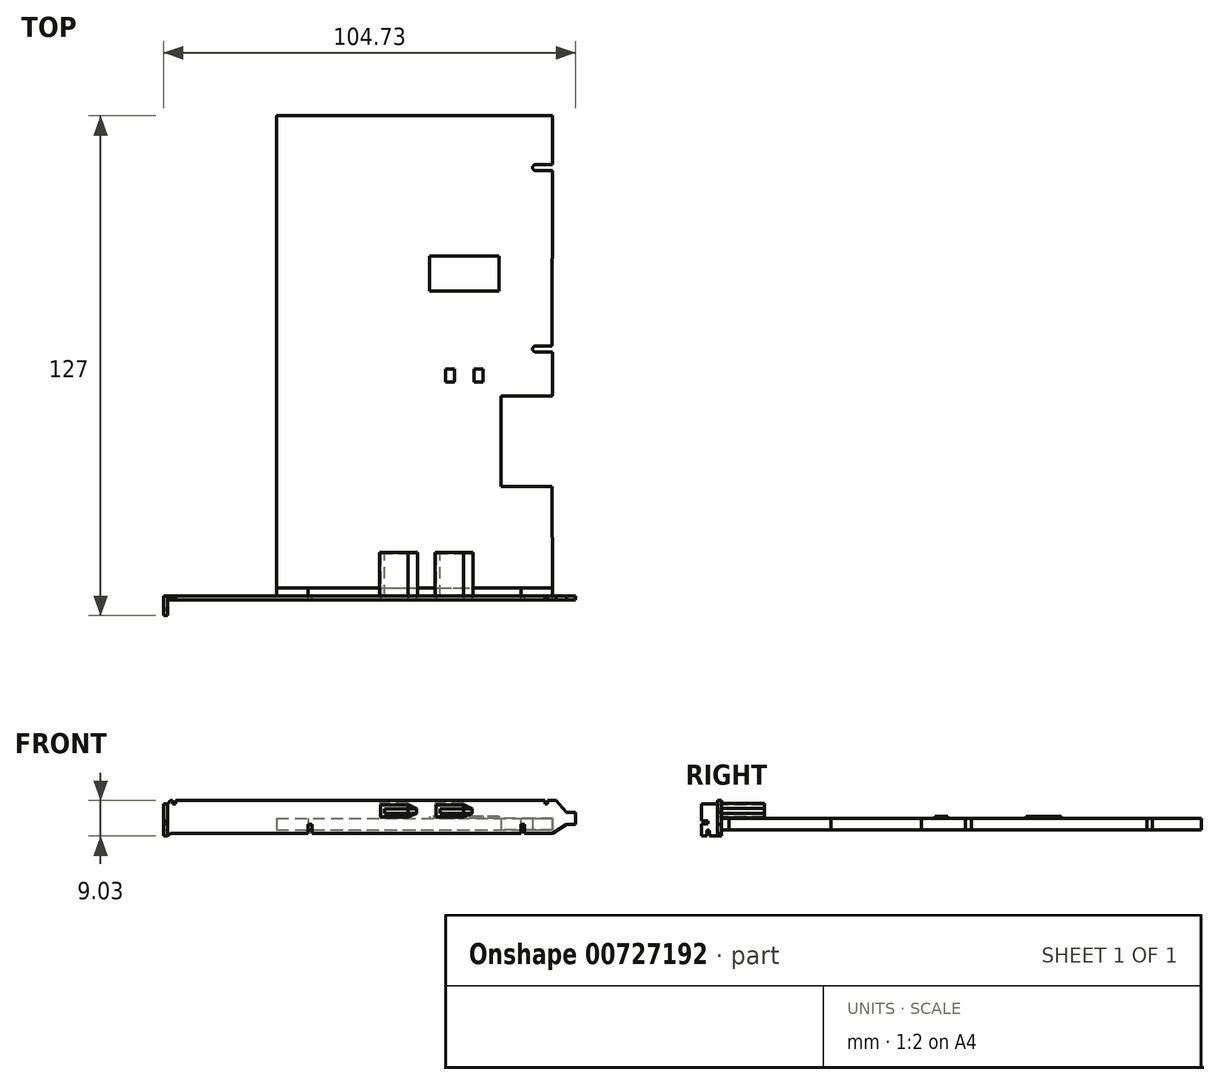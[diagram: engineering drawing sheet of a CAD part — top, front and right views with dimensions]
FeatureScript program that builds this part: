
annotation { "Feature Type Name" : "Feature", "Feature Type Description" : "" }
export const myFeature = defineFeature(function(context is Context, id is Id, definition is map)
    precondition{}
    {
        {
            var Q0;
            Q0=qCreatedBy(makeId("Top.planeOp"),FACE);
            var sketch = newSketch(context, id + "F0", { "sketchPlane" : qUnion([Q0])});
            skLineSegment(sketch, "E0.bottom", {"start": v(-33.4, 60) * mm, "end": v(36.6, 60) * mm});
            skLineSegment(sketch, "E0.top", {"start": v(-33.4, -60) * mm, "end": v(36.6, -60) * mm});
            skLineSegment(sketch, "E0.left", {"start": v(-33.4, 60) * mm, "end": v(-33.4, -60) * mm});
            skPoint(sketch, "E0.middle", {"position": v(1.6, 0) * mm});
            skLineSegment(sketch, "E1.bottom", {"start": v(36.55, -11.18) * mm, "end": v(36.6, -11.18) * mm});
            skLineSegment(sketch, "E1.top", {"start": v(36.6, -26.7) * mm, "end": v(36.6, -26.7) * mm});
            skLineSegment(sketch, "E2", {"start": v(36.6, 60) * mm, "end": v(36.6, 47.56) * mm});
            skLineSegment(sketch, "E3.bottom", {"start": v(36.55, -11.18) * mm, "end": v(23.55, -11.18) * mm});
            skLineSegment(sketch, "E3.top", {"start": v(36.55, -34.18) * mm, "end": v(23.55, -34.18) * mm});
            skLineSegment(sketch, "E3.right", {"start": v(23.55, -11.18) * mm, "end": v(23.55, -34.18) * mm});
            skLineSegment(sketch, "E4", {"start": v(36.6, -60) * mm, "end": v(36.55, -34.18) * mm});
            skLineSegment(sketch, "E5", {"start": v(36.6, 0) * mm, "end": v(32.35, 0) * mm});
            skLineSegment(sketch, "E6", {"start": v(31.6, 0.75) * mm, "end": v(31.6, 0.75) * mm});
            skLineSegment(sketch, "E7", {"start": v(32.35, 1.5) * mm, "end": v(36.55, 1.5) * mm});
            skLineSegment(sketch, "E8", {"start": v(36.6, 47.56) * mm, "end": v(32.35, 47.56) * mm});
            skLineSegment(sketch, "E9", {"start": v(31.6, 46.81) * mm, "end": v(31.6, 46.81) * mm});
            skLineSegment(sketch, "E10", {"start": v(32.35, 46.06) * mm, "end": v(36.6, 46.06) * mm});
            skLineSegment(sketch, "E11.trimOffspring", {"start": v(36.6, 0) * mm, "end": v(36.6, -11.18) * mm});
            skLineSegment(sketch, "E12", {"start": v(36.55, 1.5) * mm, "end": v(36.6, 46.06) * mm});
            skPoint(sketch, "E13.visualSharp", {"position": v(31.6, 47.56) * mm});
            skArc(sketch, "E13.filletArc", {"start": v(32.35, 47.56) * mm, "mid": v(31.82, 47.34) * mm, "end": v(31.6, 46.81) * mm});
            skPoint(sketch, "E14.visualSharp", {"position": v(31.6, 46.06) * mm});
            skArc(sketch, "E14.filletArc", {"start": v(31.6, 46.81) * mm, "mid": v(31.82, 46.28) * mm, "end": v(32.35, 46.06) * mm});
            skPoint(sketch, "E15.visualSharp", {"position": v(31.6, 0) * mm});
            skArc(sketch, "E15.filletArc", {"start": v(31.6, 0.75) * mm, "mid": v(31.82, 0.22) * mm, "end": v(32.35, 0) * mm});
            skPoint(sketch, "E16.visualSharp", {"position": v(31.6, 1.5) * mm});
            skArc(sketch, "E16.filletArc", {"start": v(32.35, 1.5) * mm, "mid": v(31.82, 1.28) * mm, "end": v(31.6, 0.75) * mm});
            skSolve(sketch);
        }
        {
            var Q0;
            Q0 = qSketchRegion(id + "F0", true);
            extrude(context, id + "F1", {"entities" : qUnion([Q0]), "depth" : 3 * mm, "offsetDistance" : 25 * mm});
        }
        {
            var Q0;
            Q0=makeQuery(id+"F1.opExtrude","SWEPT_FACE",FACE,{"disambiguationData":[OSD([sQuery(id+"F0.wireOp",EDGE,"E0.top")])]});
            var sketch = newSketch(context, id + "F2", { "sketchPlane" : qUnion([Q0])});
            skLineSegment(sketch, "E17.bottom", {"start": v(36.6, 0) * mm, "end": v(28.6, 0) * mm});
            skLineSegment(sketch, "E17.top", {"start": v(36.6, 3) * mm, "end": v(28.6, 3) * mm});
            skLineSegment(sketch, "E17.left", {"start": v(36.6, 0) * mm, "end": v(36.6, 3) * mm});
            skLineSegment(sketch, "E17.right", {"start": v(28.6, 0) * mm, "end": v(28.6, 3) * mm});
            skLineSegment(sketch, "E18.bottom", {"start": v(-33.4, 3) * mm, "end": v(-25.4, 3) * mm});
            skLineSegment(sketch, "E18.top", {"start": v(-33.4, 0) * mm, "end": v(-25.4, 0) * mm});
            skLineSegment(sketch, "E18.left", {"start": v(-33.4, 3) * mm, "end": v(-33.4, 0) * mm});
            skLineSegment(sketch, "E18.right", {"start": v(-25.4, 3) * mm, "end": v(-25.4, 0) * mm});
            skSolve(sketch);
        }
        {
            var Q0;
            Q0 = qSketchRegion(id + "F2", true);
            extrude(context, id + "F3", {"entities" : qUnion([Q0]), "depth" : 2 * mm, "offsetDistance" : 25 * mm});
        }
        {
            var Q0;
            Q0=makeQuery(id+"F3.opExtrude","CAP_FACE",FACE,{"disambiguationData":[OSD([sQuery(id+"F2.wireOp",EDGE,"E18.bottom"),sQuery(id+"F2.wireOp",EDGE,"E18.top"),sQuery(id+"F2.wireOp",EDGE,"E18.left"),sQuery(id+"F2.wireOp",EDGE,"E18.right")])],"isStart":false});
            var sketch = newSketch(context, id + "F4", { "sketchPlane" : qUnion([Q0])});
            skLineSegment(sketch, "E19", {"start": v(-25.4, 0) * mm, "end": v(-25.4, 1.5) * mm});
            skLineSegment(sketch, "E20", {"start": v(-25.4, 1.5) * mm, "end": v(-24.4, 1.5) * mm});
            skLineSegment(sketch, "E21", {"start": v(-24.4, 1.5) * mm, "end": v(-24.4, -0.8) * mm});
            skLineSegment(sketch, "E22", {"start": v(28.6, 0) * mm, "end": v(28.6, 0.1) * mm});
            skPoint(sketch, "E23.end.orphan", {"position": v(28.6, -0.8) * mm});
            skLineSegment(sketch, "E24", {"start": v(-24.4, -0.8) * mm, "end": v(28.6, -0.8) * mm});
            skLineSegment(sketch, "E25", {"start": v(28.6, -0.8) * mm, "end": v(28.6, 1.5) * mm});
            skLineSegment(sketch, "E26", {"start": v(28.6, 1.5) * mm, "end": v(29.6, 1.5) * mm});
            skLineSegment(sketch, "E27", {"start": v(29.6, 1.5) * mm, "end": v(29.6, 0) * mm});
            skPoint(sketch, "E27.endSnap0", {"position": v(-29.4, 0) * mm});
            skLineSegment(sketch, "E28", {"start": v(-25.4, 0) * mm, "end": v(-25.4, -0.8) * mm});
            skLineSegment(sketch, "E29", {"start": v(-25.4, -0.8) * mm, "end": v(-60.4, -0.8) * mm});
            skLineSegment(sketch, "E30", {"start": v(29.6, 0) * mm, "end": v(29.6, -0.8) * mm});
            skLineSegment(sketch, "E31", {"start": v(29.6, -0.8) * mm, "end": v(36.6, -0.8) * mm});
            skLineSegment(sketch, "E32", {"start": v(36.6, -0.8) * mm, "end": v(40.24, 1.5) * mm});
            skLineSegment(sketch, "E33", {"start": v(40.24, 1.5) * mm, "end": v(42.54, 1.5) * mm});
            skLineSegment(sketch, "E34", {"start": v(42.54, 1.5) * mm, "end": v(42.54, 4.54) * mm});
            skLineSegment(sketch, "E35", {"start": v(42.54, 4.54) * mm, "end": v(40.24, 4.54) * mm});
            skLineSegment(sketch, "E36", {"start": v(40.24, 4.54) * mm, "end": v(37.54, 7.5) * mm});
            skLineSegment(sketch, "E37", {"start": v(37.54, 7.5) * mm, "end": v(35.44, 7.5) * mm});
            skLineSegment(sketch, "E38", {"start": v(35.44, 7.5) * mm, "end": v(35.44, 6.6) * mm});
            skLineSegment(sketch, "E39", {"start": v(35.44, 6.6) * mm, "end": v(34.74, 6.6) * mm});
            skLineSegment(sketch, "E40", {"start": v(34.74, 6.6) * mm, "end": v(34.74, 7.5) * mm});
            skLineSegment(sketch, "E41", {"start": v(34.74, 7.5) * mm, "end": v(-59.13, 7.5) * mm});
            skLineSegment(sketch, "E42", {"start": v(-59.13, 7.5) * mm, "end": v(-59.13, 6.6) * mm});
            skLineSegment(sketch, "E43", {"start": v(-59.13, 6.6) * mm, "end": v(-59.83, 6.6) * mm});
            skLineSegment(sketch, "E44", {"start": v(-59.83, 6.6) * mm, "end": v(-59.83, 7.5) * mm});
            skLineSegment(sketch, "E45.trimOffspring", {"start": v(-59.83, 7.5) * mm, "end": v(-60.4, 7.5) * mm});
            skLineSegment(sketch, "E46", {"start": v(-60.4, -0.8) * mm, "end": v(-61.16, -1.54) * mm});
            skLineSegment(sketch, "E47", {"start": v(-60.4, 7.5) * mm, "end": v(-61.16, 6.6) * mm});
            skLineSegment(sketch, "E48", {"start": v(-61.16, 6.6) * mm, "end": v(-62.19, 6.6) * mm});
            skLineSegment(sketch, "E49", {"start": v(-62.19, 6.6) * mm, "end": v(-62.19, -1.54) * mm});
            skLineSegment(sketch, "E50", {"start": v(-62.19, -1.54) * mm, "end": v(-61.16, -1.54) * mm});
            skSolve(sketch);
        }
        {
            var Q0;
            Q0 = qSketchRegion(id + "F4", true);
            extrude(context, id + "F5", {"entities" : qUnion([Q0]), "depth" : 1 * mm, "offsetDistance" : 25 * mm});
        }
        {
            var Q0;
            Q0=makeQuery(id+"F5.opExtrude","CAP_FACE",FACE,{"disambiguationData":[OSD([sQuery(id+"F4.wireOp",EDGE,"E19"),sQuery(id+"F4.wireOp",EDGE,"E20"),sQuery(id+"F4.wireOp",EDGE,"E21"),sQuery(id+"F4.wireOp",EDGE,"E24"),sQuery(id+"F4.wireOp",EDGE,"E25"),sQuery(id+"F4.wireOp",EDGE,"E26"),sQuery(id+"F4.wireOp",EDGE,"E27"),sQuery(id+"F4.wireOp",EDGE,"E28"),sQuery(id+"F4.wireOp",EDGE,"E29"),sQuery(id+"F4.wireOp",EDGE,"E30"),sQuery(id+"F4.wireOp",EDGE,"E31"),sQuery(id+"F4.wireOp",EDGE,"E32"),sQuery(id+"F4.wireOp",EDGE,"E33"),sQuery(id+"F4.wireOp",EDGE,"E34"),sQuery(id+"F4.wireOp",EDGE,"E35"),sQuery(id+"F4.wireOp",EDGE,"E36"),sQuery(id+"F4.wireOp",EDGE,"E37"),sQuery(id+"F4.wireOp",EDGE,"E38"),sQuery(id+"F4.wireOp",EDGE,"E39"),sQuery(id+"F4.wireOp",EDGE,"E40"),sQuery(id+"F4.wireOp",EDGE,"E41"),sQuery(id+"F4.wireOp",EDGE,"E42"),sQuery(id+"F4.wireOp",EDGE,"E43"),sQuery(id+"F4.wireOp",EDGE,"E44"),sQuery(id+"F4.wireOp",EDGE,"E45.trimOffspring"),sQuery(id+"F4.wireOp",EDGE,"E46"),sQuery(id+"F4.wireOp",EDGE,"E47"),sQuery(id+"F4.wireOp",EDGE,"E48"),sQuery(id+"F4.wireOp",EDGE,"E49"),sQuery(id+"F4.wireOp",EDGE,"E50")])],"isStart":false});
            var sketch = newSketch(context, id + "F6", { "sketchPlane" : qUnion([Q0])});
            skLineSegment(sketch, "E51", {"start": v(16.19, 3.63) * mm, "end": v(16.19, 3.63) * mm});
            skLineSegment(sketch, "E52", {"start": v(16.19, 5.43) * mm, "end": v(16.19, 4.3) * mm});
            skLineSegment(sketch, "E53", {"start": v(16.19, 4.3) * mm, "end": v(14.06, 3.3) * mm});
            skLineSegment(sketch, "E54.MirrorCS", {"start": v(16.19, 5.43) * mm, "end": v(14.06, 6.43) * mm});
            skPoint(sketch, "E55.orphan", {"position": v(16.19, 3.63) * mm});
            skPoint(sketch, "E56.orphan", {"position": v(16.19, 6.1) * mm});
            skLineSegment(sketch, "E57", {"start": v(14.06, 3.3) * mm, "end": v(7.06, 3.3) * mm});
            skLineSegment(sketch, "E58", {"start": v(14.06, 6.43) * mm, "end": v(7.06, 6.43) * mm});
            skLineSegment(sketch, "E59", {"start": v(7.06, 6.43) * mm, "end": v(7.06, 3.3) * mm});
            skPoint(sketch, "E60.end.orphan", {"position": v(18.65, 3.3) * mm});
            skLineSegment(sketch, "E61", {"start": v(0, 6.43) * mm, "end": v(-7, 6.43) * mm});
            skLineSegment(sketch, "E62", {"start": v(0, 3.3) * mm, "end": v(-7, 3.3) * mm});
            skLineSegment(sketch, "E63", {"start": v(-7, 6.43) * mm, "end": v(-7, 3.3) * mm});
            skLineSegment(sketch, "E64", {"start": v(0, 3.3) * mm, "end": v(2.1, 4.3) * mm});
            skLineSegment(sketch, "E65", {"start": v(0, 6.43) * mm, "end": v(2.1, 5.43) * mm});
            skLineSegment(sketch, "E66", {"start": v(2.1, 5.43) * mm, "end": v(2.1, 4.3) * mm});
            skPoint(sketch, "E67.orphan", {"position": v(-2.37, 5.43) * mm});
            skPoint(sketch, "E68.orphan", {"position": v(-2.37, 4.3) * mm});
            skSolve(sketch);
        }
        {
            var Q0;
            Q0 = qSketchRegion(id + "F6", true);
            extrude(context, id + "F7", {"entities" : qUnion([Q0]), "operationType" : NewBodyOperationType.REMOVE, "oppositeDirection" : true, "depth" : 25 * mm, "offsetDistance" : 25 * mm});
        }
        {
            var Q0;
            Q0=makeQuery(id+"F5.opExtrude","CAP_FACE",FACE,{"disambiguationData":[OSD([sQuery(id+"F4.wireOp",EDGE,"E19"),sQuery(id+"F4.wireOp",EDGE,"E20"),sQuery(id+"F4.wireOp",EDGE,"E21"),sQuery(id+"F4.wireOp",EDGE,"E24"),sQuery(id+"F4.wireOp",EDGE,"E25"),sQuery(id+"F4.wireOp",EDGE,"E26"),sQuery(id+"F4.wireOp",EDGE,"E27"),sQuery(id+"F4.wireOp",EDGE,"E28"),sQuery(id+"F4.wireOp",EDGE,"E29"),sQuery(id+"F4.wireOp",EDGE,"E30"),sQuery(id+"F4.wireOp",EDGE,"E31"),sQuery(id+"F4.wireOp",EDGE,"E32"),sQuery(id+"F4.wireOp",EDGE,"E33"),sQuery(id+"F4.wireOp",EDGE,"E34"),sQuery(id+"F4.wireOp",EDGE,"E35"),sQuery(id+"F4.wireOp",EDGE,"E36"),sQuery(id+"F4.wireOp",EDGE,"E37"),sQuery(id+"F4.wireOp",EDGE,"E38"),sQuery(id+"F4.wireOp",EDGE,"E39"),sQuery(id+"F4.wireOp",EDGE,"E40"),sQuery(id+"F4.wireOp",EDGE,"E41"),sQuery(id+"F4.wireOp",EDGE,"E42"),sQuery(id+"F4.wireOp",EDGE,"E43"),sQuery(id+"F4.wireOp",EDGE,"E44"),sQuery(id+"F4.wireOp",EDGE,"E45.trimOffspring"),sQuery(id+"F4.wireOp",EDGE,"E46"),sQuery(id+"F4.wireOp",EDGE,"E47"),sQuery(id+"F4.wireOp",EDGE,"E48"),sQuery(id+"F4.wireOp",EDGE,"E49"),sQuery(id+"F4.wireOp",EDGE,"E50")])],"isStart":true});
            var sketch = newSketch(context, id + "F8", { "sketchPlane" : qUnion([Q0])});
            skLineSegment(sketch, "E69", {"start": v(0, 6.43) * mm, "end": v(7, 6.43) * mm});
            skLineSegment(sketch, "E70", {"start": v(7, 6.43) * mm, "end": v(7, 3.3) * mm});
            skLineSegment(sketch, "E71", {"start": v(7, 3.3) * mm, "end": v(0, 3.3) * mm});
            skLineSegment(sketch, "E72", {"start": v(0, 3.3) * mm, "end": v(-2.1, 4.3) * mm});
            skLineSegment(sketch, "E73", {"start": v(-2.1, 4.3) * mm, "end": v(-2.1, 5.43) * mm});
            skLineSegment(sketch, "E74", {"start": v(-2.1, 5.43) * mm, "end": v(0, 6.43) * mm});
            skLineSegment(sketch, "E75", {"start": v(3.31, 6.73) * mm, "end": v(7.3, 6.73) * mm});
            skLineSegment(sketch, "E76", {"start": v(7.3, 6.73) * mm, "end": v(7.3, 3.1) * mm});
            skLineSegment(sketch, "E77", {"start": v(7.3, 3.1) * mm, "end": v(0, 3.1) * mm});
            skLineSegment(sketch, "E78", {"start": v(0, 3.1) * mm, "end": v(-2.4, 4.3) * mm});
            skLineSegment(sketch, "E79", {"start": v(-2.4, 4.3) * mm, "end": v(-2.4, 5.56) * mm});
            skLineSegment(sketch, "E80", {"start": v(-2.4, 5.56) * mm, "end": v(0.06, 6.73) * mm});
            skLineSegment(sketch, "E81", {"start": v(0.06, 6.73) * mm, "end": v(3.31, 6.73) * mm});
            skPoint(sketch, "E82.end.orphan", {"position": v(3.24, 3.1) * mm});
            skPoint(sketch, "E83.end.orphan", {"position": v(7.3, 4.86) * mm});
            skPoint(sketch, "E83.start.orphan", {"position": v(7, 4.86) * mm});
            skPoint(sketch, "E84.orphan", {"position": v(-1.05, 5.93) * mm});
            skPoint(sketch, "E85.end.orphan", {"position": v(-2.4, 4.86) * mm});
            skPoint(sketch, "E85.start.orphan", {"position": v(-2.1, 4.86) * mm});
            skSolve(sketch);
        }
        {
            var Q0;
            Q0 = qSketchRegion(id + "F8", true);
            extrude(context, id + "F9", {"entities" : qUnion([Q0]), "operationType" : NewBodyOperationType.ADD, "depth" : 11 * mm, "offsetDistance" : 25 * mm});
        }
        {
            var Q0;
            Q0=makeQuery(id+"F5.opExtrude","CAP_FACE",FACE,{"disambiguationData":[OSD([sQuery(id+"F4.wireOp",EDGE,"E19"),sQuery(id+"F4.wireOp",EDGE,"E20"),sQuery(id+"F4.wireOp",EDGE,"E21"),sQuery(id+"F4.wireOp",EDGE,"E24"),sQuery(id+"F4.wireOp",EDGE,"E25"),sQuery(id+"F4.wireOp",EDGE,"E26"),sQuery(id+"F4.wireOp",EDGE,"E27"),sQuery(id+"F4.wireOp",EDGE,"E28"),sQuery(id+"F4.wireOp",EDGE,"E29"),sQuery(id+"F4.wireOp",EDGE,"E30"),sQuery(id+"F4.wireOp",EDGE,"E31"),sQuery(id+"F4.wireOp",EDGE,"E32"),sQuery(id+"F4.wireOp",EDGE,"E33"),sQuery(id+"F4.wireOp",EDGE,"E34"),sQuery(id+"F4.wireOp",EDGE,"E35"),sQuery(id+"F4.wireOp",EDGE,"E36"),sQuery(id+"F4.wireOp",EDGE,"E37"),sQuery(id+"F4.wireOp",EDGE,"E38"),sQuery(id+"F4.wireOp",EDGE,"E39"),sQuery(id+"F4.wireOp",EDGE,"E40"),sQuery(id+"F4.wireOp",EDGE,"E41"),sQuery(id+"F4.wireOp",EDGE,"E42"),sQuery(id+"F4.wireOp",EDGE,"E43"),sQuery(id+"F4.wireOp",EDGE,"E44"),sQuery(id+"F4.wireOp",EDGE,"E45.trimOffspring"),sQuery(id+"F4.wireOp",EDGE,"E46"),sQuery(id+"F4.wireOp",EDGE,"E47"),sQuery(id+"F4.wireOp",EDGE,"E48"),sQuery(id+"F4.wireOp",EDGE,"E49"),sQuery(id+"F4.wireOp",EDGE,"E50")])],"isStart":true});
            var sketch = newSketch(context, id + "F10", { "sketchPlane" : qUnion([Q0])});
            skLineSegment(sketch, "E86", {"start": v(-14.09, 6.43) * mm, "end": v(-7.09, 6.43) * mm});
            skLineSegment(sketch, "E87", {"start": v(-7.09, 6.43) * mm, "end": v(-7.09, 3.3) * mm});
            skLineSegment(sketch, "E88", {"start": v(-7.09, 3.3) * mm, "end": v(-14.09, 3.3) * mm});
            skLineSegment(sketch, "E89", {"start": v(-14.09, 3.3) * mm, "end": v(-16.19, 4.3) * mm});
            skLineSegment(sketch, "E90", {"start": v(-16.19, 4.3) * mm, "end": v(-16.19, 5.43) * mm});
            skLineSegment(sketch, "E91", {"start": v(-16.19, 5.43) * mm, "end": v(-14.09, 6.43) * mm});
            skLineSegment(sketch, "E92", {"start": v(-10.78, 6.73) * mm, "end": v(-6.79, 6.73) * mm});
            skLineSegment(sketch, "E93", {"start": v(-6.79, 6.73) * mm, "end": v(-6.79, 3.1) * mm});
            skLineSegment(sketch, "E94", {"start": v(-6.79, 3.1) * mm, "end": v(-14.09, 3.1) * mm});
            skLineSegment(sketch, "E95", {"start": v(-14.09, 3.1) * mm, "end": v(-16.49, 4.3) * mm});
            skLineSegment(sketch, "E96", {"start": v(-16.49, 4.3) * mm, "end": v(-16.49, 5.56) * mm});
            skLineSegment(sketch, "E97", {"start": v(-16.49, 5.56) * mm, "end": v(-14.02, 6.73) * mm});
            skLineSegment(sketch, "E98", {"start": v(-14.02, 6.73) * mm, "end": v(-10.78, 6.73) * mm});
            skPoint(sketch, "E99.end.orphan", {"position": v(-10.85, 3.1) * mm});
            skPoint(sketch, "E100.end.orphan", {"position": v(-6.79, 4.87) * mm});
            skPoint(sketch, "E100.start.orphan", {"position": v(-7.09, 4.87) * mm});
            skPoint(sketch, "E101.orphan", {"position": v(-15.14, 5.93) * mm});
            skPoint(sketch, "E102.end.orphan", {"position": v(-16.49, 4.87) * mm});
            skPoint(sketch, "E102.start.orphan", {"position": v(-16.19, 4.87) * mm});
            skSolve(sketch);
        }
        {
            var Q0;
            {var subQ11=sQuery(id+"F10.wireOp",EDGE,"E86");Q0=makeQuery(id+"F10.imprint","IMPRINT",FACE,{"disambiguationData":[TD([[makeQuery(id+"F10.imprint","IMPRINT",EDGE,{"derivedFrom":subQ11}),1.0]])]});}
            extrude(context, id + "F11", {"entities" : qUnion([Q0]), "operationType" : NewBodyOperationType.ADD, "depth" : 11 * mm, "offsetDistance" : 25 * mm});
        }
        {
            var Q0;
            Q0=makeQuery(id+"F9.boolean.opBoolean","MERGE",FACE,{"derivedFrom":[makeQuery(id+"F7.boolean.opBoolean","COPY",FACE,{"derivedFrom":makeQuery(id+"F7.opExtrude","SWEPT_FACE",FACE,{"disambiguationData":[OSD([sQuery(id+"F6.wireOp",EDGE,"E62")])]})}),makeQuery(id+"F9.opExtrude","SWEPT_FACE",FACE,{"disambiguationData":[OSD([sQuery(id+"F8.wireOp",EDGE,"E71")])]})]});
            var sketch = newSketch(context, id + "F12", { "sketchPlane" : qUnion([Q0])});
            skLineSegment(sketch, "E103", {"start": v(-7, -51) * mm, "end": v(0, -51) * mm});
            skLineSegment(sketch, "E104", {"start": v(0, -51) * mm, "end": v(0, -51.2) * mm});
            skLineSegment(sketch, "E105", {"start": v(0, -51.2) * mm, "end": v(-7, -51.2) * mm});
            skLineSegment(sketch, "E106", {"start": v(-7, -51.2) * mm, "end": v(-7, -51) * mm});
            skSolve(sketch);
        }
        {
            var Q0;
            Q0 = qSketchRegion(id + "F12", true);
            extrude(context, id + "F13", {"entities" : qUnion([Q0]), "operationType" : NewBodyOperationType.ADD, "depth" : 3.2 * mm, "offsetDistance" : 25 * mm});
        }
        {
            var Q0;
            Q0=makeQuery(id+"F9.boolean.opBoolean","MERGE",FACE,{"derivedFrom":[makeQuery(id+"F7.boolean.opBoolean","COPY",FACE,{"derivedFrom":makeQuery(id+"F7.opExtrude","SWEPT_FACE",FACE,{"disambiguationData":[OSD([sQuery(id+"F6.wireOp",EDGE,"E66")])]})}),makeQuery(id+"F9.opExtrude","SWEPT_FACE",FACE,{"disambiguationData":[OSD([sQuery(id+"F8.wireOp",EDGE,"E73")])]})]});
            var sketch = newSketch(context, id + "F14", { "sketchPlane" : qUnion([Q0])});
            skLineSegment(sketch, "E107", {"start": v(51, 4.3) * mm, "end": v(51, 5.43) * mm});
            skLineSegment(sketch, "E108", {"start": v(51, 5.43) * mm, "end": v(51.2, 5.43) * mm});
            skLineSegment(sketch, "E109", {"start": v(51.2, 5.43) * mm, "end": v(51.2, 4.3) * mm});
            skLineSegment(sketch, "E110", {"start": v(51.2, 4.3) * mm, "end": v(51, 4.3) * mm});
            skSolve(sketch);
        }
        {
            var Q0;
            Q0 = qSketchRegion(id + "F14", true);
            extrude(context, id + "F15", {"entities" : qUnion([Q0]), "operationType" : NewBodyOperationType.ADD, "depth" : 5.5 * mm, "offsetDistance" : 25 * mm});
        }
        {
            var Q0;
            {var subQ0=sQuery(id+"F6.wireOp",EDGE,"E57");Q0=makeQuery(id+"F11.boolean.opBoolean","MERGE",FACE,{"derivedFrom":[makeQuery(id+"F7.boolean.opBoolean","COPY",FACE,{"derivedFrom":makeQuery(id+"F7.opExtrude","SWEPT_FACE",FACE,{"disambiguationData":[OSD([subQ0])]})}),makeQuery(id+"F11.opExtrude","SWEPT_FACE",FACE,{"disambiguationData":[OSD([sQuery(id+"F4.wireOp",EDGE,"E19"),sQuery(id+"F4.wireOp",EDGE,"E20"),sQuery(id+"F4.wireOp",EDGE,"E21"),sQuery(id+"F4.wireOp",EDGE,"E24"),sQuery(id+"F4.wireOp",EDGE,"E25"),sQuery(id+"F4.wireOp",EDGE,"E26"),sQuery(id+"F4.wireOp",EDGE,"E27"),sQuery(id+"F4.wireOp",EDGE,"E28"),sQuery(id+"F4.wireOp",EDGE,"E29"),sQuery(id+"F4.wireOp",EDGE,"E30"),sQuery(id+"F4.wireOp",EDGE,"E31"),sQuery(id+"F4.wireOp",EDGE,"E32"),sQuery(id+"F4.wireOp",EDGE,"E33"),sQuery(id+"F4.wireOp",EDGE,"E34"),sQuery(id+"F4.wireOp",EDGE,"E35"),sQuery(id+"F4.wireOp",EDGE,"E36"),sQuery(id+"F4.wireOp",EDGE,"E37"),sQuery(id+"F4.wireOp",EDGE,"E38"),sQuery(id+"F4.wireOp",EDGE,"E39"),sQuery(id+"F4.wireOp",EDGE,"E40"),sQuery(id+"F4.wireOp",EDGE,"E41"),sQuery(id+"F4.wireOp",EDGE,"E42"),sQuery(id+"F4.wireOp",EDGE,"E43"),sQuery(id+"F4.wireOp",EDGE,"E44"),sQuery(id+"F4.wireOp",EDGE,"E45.trimOffspring"),sQuery(id+"F4.wireOp",EDGE,"E46"),sQuery(id+"F4.wireOp",EDGE,"E47"),sQuery(id+"F4.wireOp",EDGE,"E48"),sQuery(id+"F4.wireOp",EDGE,"E49"),sQuery(id+"F4.wireOp",EDGE,"E50"),subQ0])]})]});}
            var sketch = newSketch(context, id + "F16", { "sketchPlane" : qUnion([Q0])});
            skLineSegment(sketch, "E111", {"start": v(7.06, -51) * mm, "end": v(14.06, -51) * mm});
            skLineSegment(sketch, "E112", {"start": v(14.06, -51) * mm, "end": v(14.06, -51.2) * mm});
            skLineSegment(sketch, "E113", {"start": v(14.06, -51.2) * mm, "end": v(7.06, -51.2) * mm});
            skLineSegment(sketch, "E114", {"start": v(7.06, -51.2) * mm, "end": v(7.06, -51) * mm});
            skSolve(sketch);
        }
        {
            var Q0;
            Q0 = qSketchRegion(id + "F16", true);
            extrude(context, id + "F17", {"entities" : qUnion([Q0]), "operationType" : NewBodyOperationType.ADD, "depth" : 3.19 * mm, "offsetDistance" : 25 * mm});
        }
        {
            var Q0;
            Q0=makeQuery(id+"F11.opExtrude","SWEPT_FACE",FACE,{"disambiguationData":[OSD([sQuery(id+"F10.wireOp",EDGE,"E90")])]});
            var sketch = newSketch(context, id + "F18", { "sketchPlane" : qUnion([Q0])});
            skLineSegment(sketch, "E115", {"start": v(51, 4.3) * mm, "end": v(51, 5.43) * mm});
            skLineSegment(sketch, "E116", {"start": v(51, 5.43) * mm, "end": v(51.2, 5.43) * mm});
            skLineSegment(sketch, "E117", {"start": v(51.2, 5.43) * mm, "end": v(51.2, 4.3) * mm});
            skLineSegment(sketch, "E118", {"start": v(51.2, 4.3) * mm, "end": v(51, 4.3) * mm});
            skSolve(sketch);
        }
        {
            var Q0;
            Q0 = qSketchRegion(id + "F18", true);
            extrude(context, id + "F19", {"entities" : qUnion([Q0]), "operationType" : NewBodyOperationType.ADD, "depth" : 7.4 * mm, "offsetDistance" : 25 * mm});
        }
        {
            var Q0;
            Q0=makeQuery(id+"F15.boolean.opBoolean","MERGE",FACE,{"derivedFrom":[makeQuery(id+"F13.opExtrude","SWEPT_FACE",FACE,{"disambiguationData":[OSD([sQuery(id+"F12.wireOp",EDGE,"E105")])]}),makeQuery(id+"F15.opExtrude","SWEPT_FACE",FACE,{"disambiguationData":[OSD([sQuery(id+"F14.wireOp",EDGE,"E109")])]})]});
            var sketch = newSketch(context, id + "F20", { "sketchPlane" : qUnion([Q0])});
            skLineSegment(sketch, "E119", {"start": v(0, 5.43) * mm, "end": v(-6, 5.43) * mm});
            skLineSegment(sketch, "E120", {"start": v(0, 4.3) * mm, "end": v(0, 5.43) * mm});
            skLineSegment(sketch, "E121", {"start": v(0, 4.3) * mm, "end": v(-6, 4.3) * mm});
            skLineSegment(sketch, "E122", {"start": v(-6, 4.3) * mm, "end": v(-6, 5.43) * mm});
            skSolve(sketch);
        }
        {
            var Q0;
            Q0 = qSketchRegion(id + "F20", true);
            extrude(context, id + "F21", {"entities" : qUnion([Q0]), "operationType" : NewBodyOperationType.ADD, "depth" : 11 * mm, "offsetDistance" : 25 * mm});
        }
        {
            var Q0;
            Q0=makeQuery(id+"F19.boolean.opBoolean","MERGE",FACE,{"derivedFrom":[makeQuery(id+"F17.opExtrude","SWEPT_FACE",FACE,{"disambiguationData":[OSD([sQuery(id+"F16.wireOp",EDGE,"E113")])]}),makeQuery(id+"F19.opExtrude","SWEPT_FACE",FACE,{"disambiguationData":[OSD([sQuery(id+"F18.wireOp",EDGE,"E117")])]})]});
            var sketch = newSketch(context, id + "F22", { "sketchPlane" : qUnion([Q0])});
            skLineSegment(sketch, "E123", {"start": v(14.06, 5.43) * mm, "end": v(8.06, 5.43) * mm});
            skLineSegment(sketch, "E124", {"start": v(14.06, 5.43) * mm, "end": v(14.06, 4.3) * mm});
            skLineSegment(sketch, "E125", {"start": v(14.06, 4.3) * mm, "end": v(8.06, 4.3) * mm});
            skLineSegment(sketch, "E126", {"start": v(8.06, 4.3) * mm, "end": v(8.06, 5.43) * mm});
            skSolve(sketch);
        }
        {
            var Q0;
            Q0 = qSketchRegion(id + "F22", true);
            extrude(context, id + "F23", {"entities" : qUnion([Q0]), "operationType" : NewBodyOperationType.ADD, "depth" : 11 * mm, "offsetDistance" : 25 * mm});
        }
        {
            var Q0;
            Q0=makeQuery(id+"F5.opExtrude","CAP_FACE",FACE,{"disambiguationData":[OSD([sQuery(id+"F4.wireOp",EDGE,"E19"),sQuery(id+"F4.wireOp",EDGE,"E20"),sQuery(id+"F4.wireOp",EDGE,"E21"),sQuery(id+"F4.wireOp",EDGE,"E24"),sQuery(id+"F4.wireOp",EDGE,"E25"),sQuery(id+"F4.wireOp",EDGE,"E26"),sQuery(id+"F4.wireOp",EDGE,"E27"),sQuery(id+"F4.wireOp",EDGE,"E28"),sQuery(id+"F4.wireOp",EDGE,"E29"),sQuery(id+"F4.wireOp",EDGE,"E30"),sQuery(id+"F4.wireOp",EDGE,"E31"),sQuery(id+"F4.wireOp",EDGE,"E32"),sQuery(id+"F4.wireOp",EDGE,"E33"),sQuery(id+"F4.wireOp",EDGE,"E34"),sQuery(id+"F4.wireOp",EDGE,"E35"),sQuery(id+"F4.wireOp",EDGE,"E36"),sQuery(id+"F4.wireOp",EDGE,"E37"),sQuery(id+"F4.wireOp",EDGE,"E38"),sQuery(id+"F4.wireOp",EDGE,"E39"),sQuery(id+"F4.wireOp",EDGE,"E40"),sQuery(id+"F4.wireOp",EDGE,"E41"),sQuery(id+"F4.wireOp",EDGE,"E42"),sQuery(id+"F4.wireOp",EDGE,"E43"),sQuery(id+"F4.wireOp",EDGE,"E44"),sQuery(id+"F4.wireOp",EDGE,"E45.trimOffspring"),sQuery(id+"F4.wireOp",EDGE,"E46"),sQuery(id+"F4.wireOp",EDGE,"E47"),sQuery(id+"F4.wireOp",EDGE,"E48"),sQuery(id+"F4.wireOp",EDGE,"E49"),sQuery(id+"F4.wireOp",EDGE,"E50")])],"isStart":false});
            var sketch = newSketch(context, id + "F24", { "sketchPlane" : qUnion([Q0])});
            skLineSegment(sketch, "E127", {"start": v(-62.19, -1.54) * mm, "end": v(-62.19, 6.6) * mm});
            skLineSegment(sketch, "E128", {"start": v(-62.19, 6.6) * mm, "end": v(-61.16, 6.6) * mm});
            skLineSegment(sketch, "E129", {"start": v(-61.16, 6.6) * mm, "end": v(-61.16, -1.54) * mm});
            skLineSegment(sketch, "E130", {"start": v(-61.16, -1.54) * mm, "end": v(-62.19, -1.54) * mm});
            skSolve(sketch);
        }
        {
            var Q0;
            Q0 = qSketchRegion(id + "F24", true);
            extrude(context, id + "F25", {"entities" : qUnion([Q0]), "operationType" : NewBodyOperationType.ADD, "depth" : 4 * mm, "offsetDistance" : 25 * mm});
        }
        {
            var Q0;
            Q0=makeQuery(id+"F25.opExtrude","SWEPT_FACE",FACE,{"disambiguationData":[OSD([sQuery(id+"F24.wireOp",EDGE,"E129")])]});
            var sketch = newSketch(context, id + "F26", { "sketchPlane" : qUnion([Q0])});
            skLineSegment(sketch, "E131", {"start": v(-65.65, -1.54) * mm, "end": v(-65.65, -0.3) * mm});
            skLineSegment(sketch, "E132", {"start": v(-65.35, 0) * mm, "end": v(-65.34, 0) * mm});
            skLineSegment(sketch, "E133", {"start": v(-65.04, -0.3) * mm, "end": v(-65.04, -1.54) * mm});
            skPoint(sketch, "E134.visualSharp", {"position": v(-65.65, 0) * mm});
            skArc(sketch, "E134.filletArc", {"start": v(-65.35, 0) * mm, "mid": v(-65.56, -0.09) * mm, "end": v(-65.65, -0.3) * mm});
            skPoint(sketch, "E135.visualSharp", {"position": v(-65.04, 0) * mm});
            skArc(sketch, "E135.filletArc", {"start": v(-65.04, -0.3) * mm, "mid": v(-65.13, -0.09) * mm, "end": v(-65.34, 0) * mm});
            skLineSegment(sketch, "E136", {"start": v(-65.65, -1.54) * mm, "end": v(-65.04, -1.54) * mm});
            skLineSegment(sketch, "E137", {"start": v(-67, 1.58) * mm, "end": v(-65.34, 1.58) * mm});
            skPoint(sketch, "E137.endSnap0", {"position": v(-65.34, -1.54) * mm});
            skLineSegment(sketch, "E138", {"start": v(-65.34, 1.58) * mm, "end": v(-65.34, 2.33) * mm});
            skLineSegment(sketch, "E139", {"start": v(-65.34, 2.33) * mm, "end": v(-67, 2.33) * mm});
            skLineSegment(sketch, "E140", {"start": v(-67, 1.58) * mm, "end": v(-67, 2.33) * mm});
            skSolve(sketch);
        }
        {
            var Q0;
            Q0 = qSketchRegion(id + "F26", true);
            extrude(context, id + "F27", {"entities" : qUnion([Q0]), "operationType" : NewBodyOperationType.REMOVE, "oppositeDirection" : true, "depth" : 25 * mm, "offsetDistance" : 25 * mm});
        }
        {
            var Q0;
            Q0=makeQuery(id+"F1.opExtrude","CAP_FACE",FACE,{"disambiguationData":[OSD([sQuery(id+"F0.wireOp",EDGE,"E0.bottom"),sQuery(id+"F0.wireOp",EDGE,"E0.top"),sQuery(id+"F0.wireOp",EDGE,"E0.left"),sQuery(id+"F0.wireOp",EDGE,"E1.bottom"),sQuery(id+"F0.wireOp",EDGE,"E2"),sQuery(id+"F0.wireOp",EDGE,"E3.bottom"),sQuery(id+"F0.wireOp",EDGE,"E3.top"),sQuery(id+"F0.wireOp",EDGE,"E3.right"),sQuery(id+"F0.wireOp",EDGE,"E4"),sQuery(id+"F0.wireOp",EDGE,"E5"),sQuery(id+"F0.wireOp",EDGE,"E7"),sQuery(id+"F0.wireOp",EDGE,"E8"),sQuery(id+"F0.wireOp",EDGE,"E10"),sQuery(id+"F0.wireOp",EDGE,"E11.trimOffspring"),sQuery(id+"F0.wireOp",EDGE,"E12"),sQuery(id+"F0.wireOp",EDGE,"E13.filletArc"),sQuery(id+"F0.wireOp",EDGE,"E14.filletArc"),sQuery(id+"F0.wireOp",EDGE,"E15.filletArc"),sQuery(id+"F0.wireOp",EDGE,"E16.filletArc")])],"isStart":false});
            var sketch = newSketch(context, id + "F28", { "sketchPlane" : qUnion([Q0])});
            skLineSegment(sketch, "E141.bottom", {"start": v(23.1, 24.36) * mm, "end": v(5.41, 24.36) * mm});
            skLineSegment(sketch, "E141.top", {"start": v(23.1, 15.4) * mm, "end": v(5.41, 15.4) * mm});
            skLineSegment(sketch, "E141.left", {"start": v(23.1, 24.36) * mm, "end": v(23.1, 15.4) * mm});
            skLineSegment(sketch, "E141.right", {"start": v(5.41, 24.36) * mm, "end": v(5.41, 15.4) * mm});
            skLineSegment(sketch, "E142.bottom", {"start": v(9.42, -4.4) * mm, "end": v(11.72, -4.4) * mm});
            skLineSegment(sketch, "E142.top", {"start": v(9.42, -7.7) * mm, "end": v(11.72, -7.7) * mm});
            skLineSegment(sketch, "E142.left", {"start": v(9.42, -4.4) * mm, "end": v(9.42, -7.7) * mm});
            skLineSegment(sketch, "E142.right", {"start": v(11.72, -4.4) * mm, "end": v(11.72, -7.7) * mm});
            skLineSegment(sketch, "E143.bottom", {"start": v(18.97, -4.4) * mm, "end": v(16.67, -4.4) * mm});
            skLineSegment(sketch, "E143.top", {"start": v(18.97, -7.7) * mm, "end": v(16.67, -7.7) * mm});
            skLineSegment(sketch, "E143.left", {"start": v(18.97, -4.4) * mm, "end": v(18.97, -7.7) * mm});
            skLineSegment(sketch, "E143.right", {"start": v(16.67, -4.4) * mm, "end": v(16.67, -7.7) * mm});
            skSolve(sketch);
        }
        {
            var Q0;
            Q0 = qSketchRegion(id + "F28", true);
            extrude(context, id + "F29", {"entities" : qUnion([Q0]), "depth" : 0.5 * mm, "offsetDistance" : 25 * mm});
        }
    });
